# Revit family: SL_Zumtobel MIREL-L A LED Q600
name_source: partatom
category: Lighting Fixtures
revit_build: Autodesk Revit 2014 (Build: 20130308_1515(x64)
units: mm (PartAtom-declared; Revit-internal decimal feet)

## types (2) — shared parameters
Apparent Load = 26 VA
Assembly Code = D5020200
Color Filter = 16777215
Description = Surface mount LED luminaire
Dimming Lamp Color Temperature Shift = <None>
Emit Shape Visible in Rendering = Yes
Emit from Rectangle Length = 600 mm
Emit from Rectangle Width = 600 mm
Height = 52 mm
Lamp = LED
Length = 600 mm
Manufacturer = Zumtobel Lighting
Tilt Angle = 90.00°
Voltage = 230 V
Width = 600 mm
zero-valued in all types: Default Elevation

## per-type parameters (varying)
| type | Model | Photometric Web File | URL |
| MIREL-L A LED Q600 Electronic | 42182127 | 42182127_(STD).IES | http://www.zumtobel.com |
| MIREL-L A LED Q600 Dimmable | 42925612 | 42925612_(STD).IES | http://www.zumtobel.de |

## geometry (parser evidence)
native form markers: Sweep x2
no freeform markers — native parametric forms only
